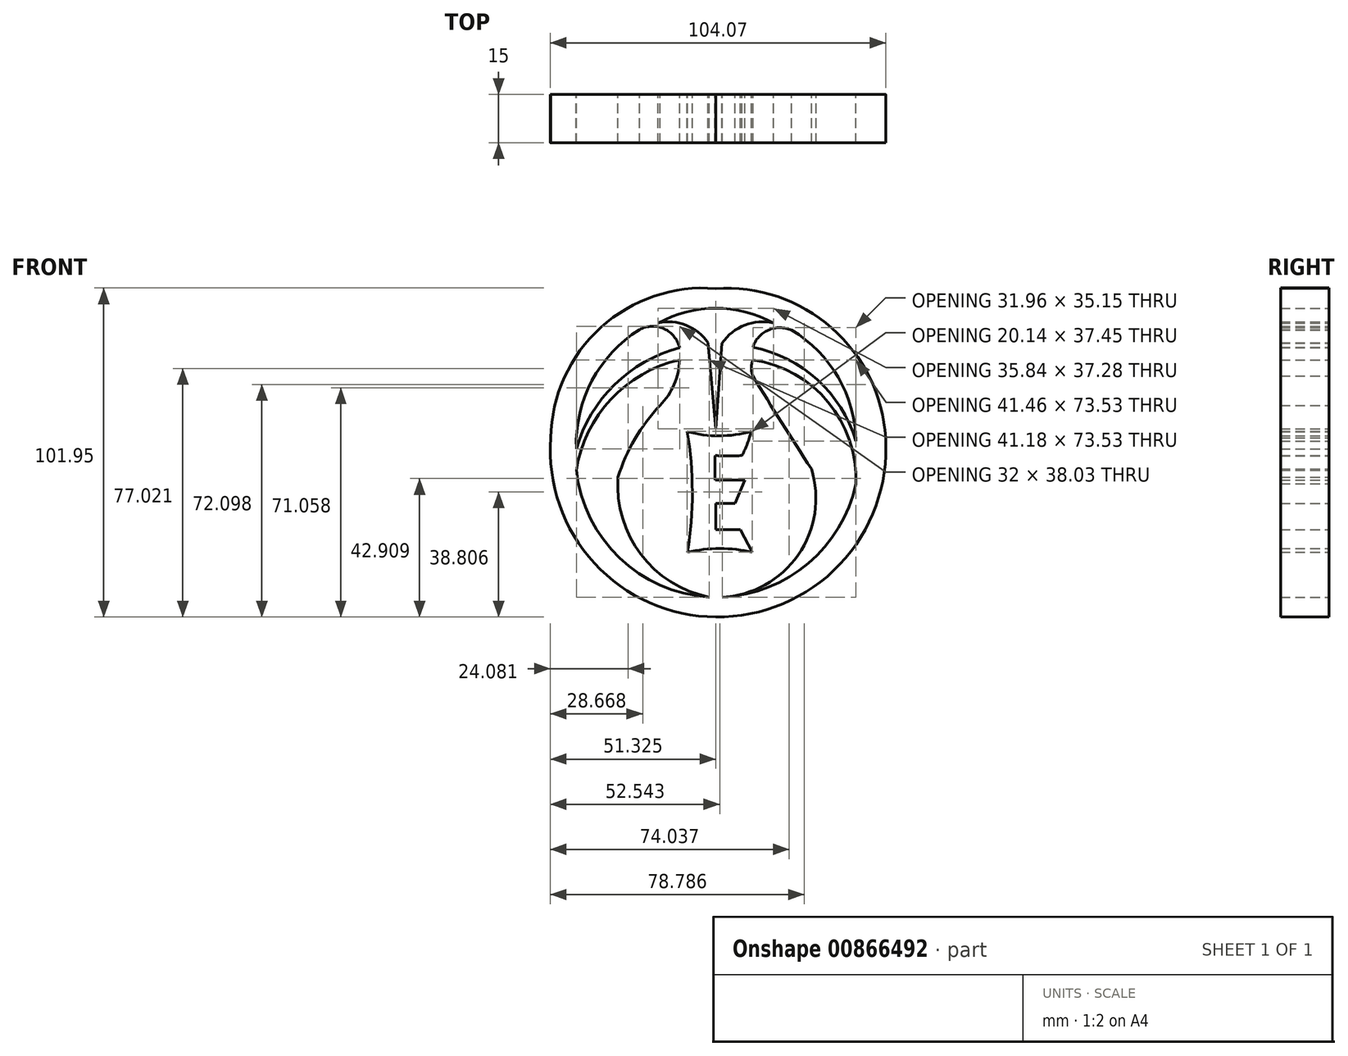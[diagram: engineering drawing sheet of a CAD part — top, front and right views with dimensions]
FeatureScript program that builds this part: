
annotation { "Feature Type Name" : "Feature", "Feature Type Description" : "" }
export const myFeature = defineFeature(function(context is Context, id is Id, definition is map)
    precondition{}
    {
        {
            var Q0;
            Q0=qCreatedBy(makeId("Front.planeOp"),FACE);
            var sketch = newSketch(context, id + "F0", { "sketchPlane" : qUnion([Q0])});
            skArc(sketch, "E0", {"start": v(0, 46.3) * mm, "mid": v(-35.58, 34.22) * mm, "end": v(-51.11, 0) * mm});
            skPoint(sketch, "E0.startSnap0", {"position": v(3.57, 46.3) * mm});
            skArc(sketch, "E1", {"start": v(-51.11, 0) * mm, "mid": v(-37.6, -38.84) * mm, "end": v(0, -55.5) * mm});
            skArc(sketch, "E2", {"start": v(0, -55.5) * mm, "mid": v(38.46, -39.25) * mm, "end": v(52.7, 0) * mm});
            skArc(sketch, "E3", {"start": v(52.7, 0) * mm, "mid": v(35.98, 34.1) * mm, "end": v(0, 46.3) * mm});
            skArc(sketch, "E4", {"start": v(-23.6, 33.52) * mm, "mid": v(-38.38, 17.67) * mm, "end": v(-43.18, -3.45) * mm});
            skArc(sketch, "E5", {"start": v(-11.18, 27.93) * mm, "mid": v(-31.35, 16.5) * mm, "end": v(-43.18, -3.45) * mm});
            skArc(sketch, "E6", {"start": v(-11.18, 27.93) * mm, "mid": v(-16, 33.83) * mm, "end": v(-23.6, 33.52) * mm});
            skArc(sketch, "E7", {"start": v(-11.18, 24.17) * mm, "mid": v(-32.46, 12) * mm, "end": v(-43.18, -10.06) * mm});
            skArc(sketch, "E8", {"start": v(-43.18, -10.06) * mm, "mid": v(-29.76, -37.21) * mm, "end": v(-2, -49.35) * mm});
            skArc(sketch, "E9", {"start": v(-30.26, -12.15) * mm, "mid": v(-23.15, -36.08) * mm, "end": v(-2, -49.35) * mm});
            skArc(sketch, "E10", {"start": v(-17.2, 10.07) * mm, "mid": v(-25, -0.3) * mm, "end": v(-30.26, -12.15) * mm});
            skArc(sketch, "E11", {"start": v(-17.2, 10.07) * mm, "mid": v(-12.89, 16.56) * mm, "end": v(-11.18, 24.17) * mm});
            skArc(sketch, "E12", {"start": v(43.5, -0.98) * mm, "mid": v(31.57, 18) * mm, "end": v(11.54, 28.12) * mm});
            skArc(sketch, "E13", {"start": v(43.5, -0.98) * mm, "mid": v(38, 18.8) * mm, "end": v(23.55, 33.39) * mm});
            skArc(sketch, "E14", {"start": v(23.55, 33.39) * mm, "mid": v(16.37, 33.43) * mm, "end": v(11.54, 28.12) * mm});
            skArc(sketch, "E15", {"start": v(43.5, -14.26) * mm, "mid": v(34.9, 11.09) * mm, "end": v(11.54, 24.17) * mm});
            skArc(sketch, "E16", {"start": v(2.05, -49.35) * mm, "mid": v(28.73, -38.84) * mm, "end": v(43.5, -14.26) * mm});
            skArc(sketch, "E17", {"start": v(2.05, -49.35) * mm, "mid": v(25.61, -36.24) * mm, "end": v(29.71, -9.58) * mm});
            skArc(sketch, "E18", {"start": v(11.54, 19.16) * mm, "mid": v(20.5, 4.72) * mm, "end": v(29.71, -9.58) * mm});
            skArc(sketch, "E19", {"start": v(11.54, 24.17) * mm, "mid": v(11.04, 21.67) * mm, "end": v(11.54, 19.16) * mm});
            skArc(sketch, "E20", {"start": v(-8.79, 1.94) * mm, "mid": v(1.13, 0.63) * mm, "end": v(11.04, 2.03) * mm});
            skPoint(sketch, "E20.endSnap0", {"position": v(11.04, 21.67) * mm});
            skArc(sketch, "E21", {"start": v(8.21, -5.45) * mm, "mid": v(9.83, -1.79) * mm, "end": v(11.04, 2.03) * mm});
            skArc(sketch, "E22", {"start": v(-0.1, -5.45) * mm, "mid": v(4.05, -5.58) * mm, "end": v(8.21, -5.45) * mm});
            skArc(sketch, "E23", {"start": v(-0.1, -5.45) * mm, "mid": v(-0.26, -9.29) * mm, "end": v(-0.1, -13.12) * mm});
            skLineSegment(sketch, "E24", {"start": v(-0.1, -13.12) * mm, "end": v(9.06, -13.12) * mm});
            skLineSegment(sketch, "E25", {"start": v(9.06, -13.12) * mm, "end": v(6, -20.26) * mm});
            skLineSegment(sketch, "E26", {"start": v(6, -20.26) * mm, "end": v(0, -20.26) * mm});
            skLineSegment(sketch, "E27", {"start": v(0, -20.26) * mm, "end": v(0, -28.36) * mm});
            skLineSegment(sketch, "E28", {"start": v(0, -28.36) * mm, "end": v(7.63, -28.36) * mm});
            skLineSegment(sketch, "E29", {"start": v(7.63, -28.36) * mm, "end": v(11.35, -35.42) * mm});
            skArc(sketch, "E30", {"start": v(11.35, -35.42) * mm, "mid": v(1.33, -34.29) * mm, "end": v(-8.7, -35.42) * mm});
            skArc(sketch, "E31", {"start": v(-8.7, -35.42) * mm, "mid": v(-7.24, -16.74) * mm, "end": v(-8.79, 1.94) * mm});
            skLineSegment(sketch, "E32", {"start": v(-2.34, 29.5) * mm, "end": v(0, 2.88) * mm});
            skLineSegment(sketch, "E33", {"start": v(0, 2.88) * mm, "end": v(2, 29.34) * mm});
            skArc(sketch, "E34", {"start": v(17.99, 35.58) * mm, "mid": v(9.03, 34.95) * mm, "end": v(2, 29.34) * mm});
            skArc(sketch, "E35", {"start": v(17.99, 35.58) * mm, "mid": v(0.06, 40.16) * mm, "end": v(-17.86, 35.58) * mm});
            skArc(sketch, "E36", {"start": v(-2.34, 29.5) * mm, "mid": v(-9.16, 34.93) * mm, "end": v(-17.86, 35.58) * mm});
            skSolve(sketch);
        }
        {
            var Q0;
            Q0=qSketchRegion(id+"F0",true);
            extrude(context, id + "F1", {"entities" : qUnion([Q0]), "depth" : 15 * mm, "offsetDistance" : 25.4 * mm});
        }
    });
